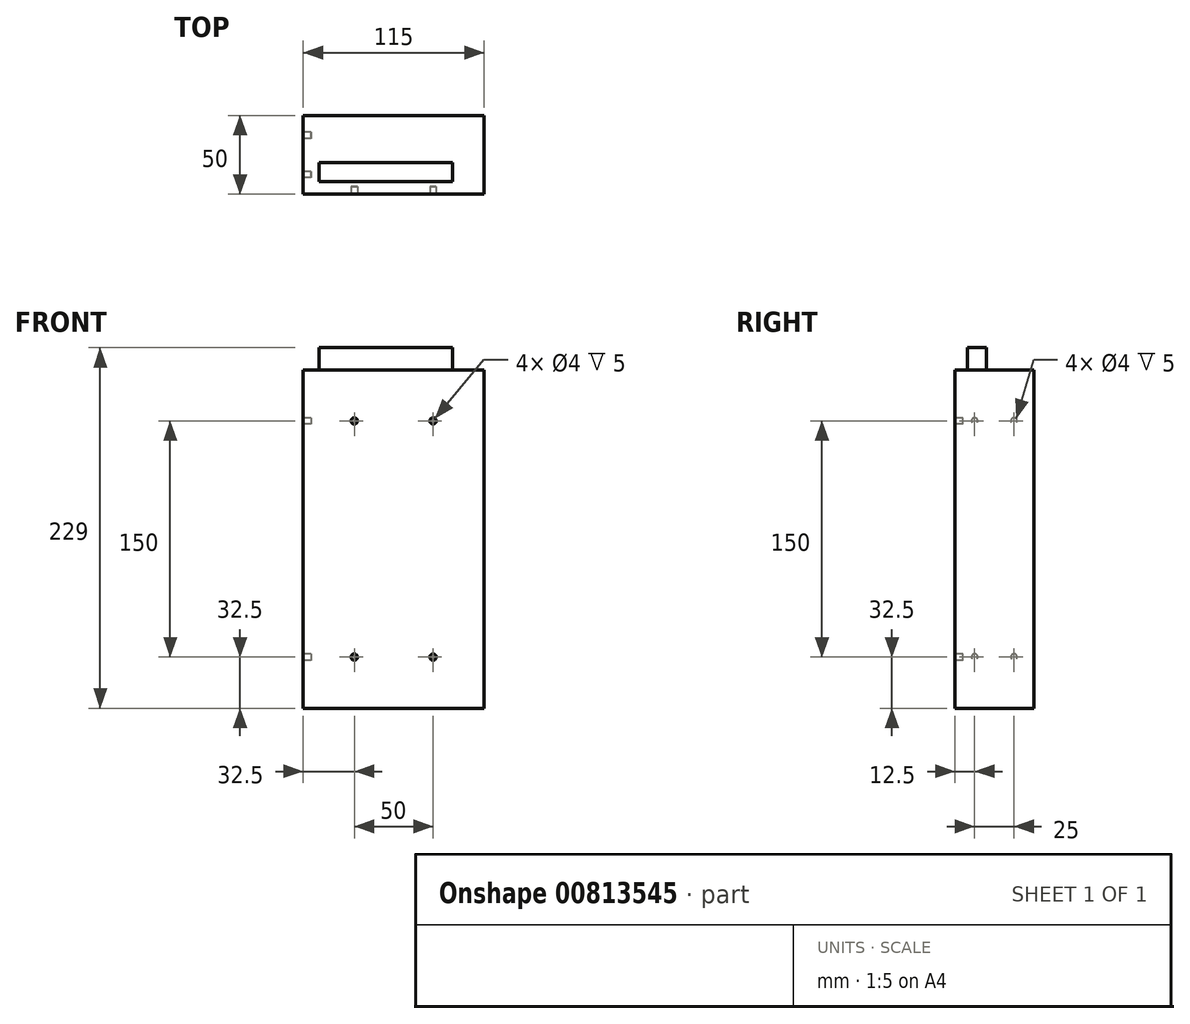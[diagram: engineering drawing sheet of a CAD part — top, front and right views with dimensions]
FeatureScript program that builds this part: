
annotation { "Feature Type Name" : "Feature", "Feature Type Description" : "" }
export const myFeature = defineFeature(function(context is Context, id is Id, definition is map)
    precondition{}
    {
        {
            var Q0;
            Q0=qCreatedBy(makeId("Front.planeOp"),FACE);
            var sketch = newSketch(context, id + "F0", { "sketchPlane" : qUnion([Q0])});
            skLineSegment(sketch, "E0.bottom", {"start": v(0, 0) * mm, "end": v(115, 0) * mm});
            skLineSegment(sketch, "E0.top", {"start": v(0, 215) * mm, "end": v(115, 215) * mm});
            skLineSegment(sketch, "E0.left", {"start": v(0, 0) * mm, "end": v(0, 215) * mm});
            skLineSegment(sketch, "E0.right", {"start": v(115, 0) * mm, "end": v(115, 215) * mm});
            skSolve(sketch);
        }
        {
            var Q0;
            Q0=makeQuery(id+"F0.imprint","IMPRINT",FACE,{"disambiguationData":[TD([[makeQuery(id+"F0.imprint","IMPRINT",EDGE,{"derivedFrom":sQuery(id+"F0.wireOp",EDGE,"E0.bottom")}),1.0]])]});
            extrude(context, id + "F1", {"entities" : qUnion([Q0]), "depth" : 50 * mm, "offsetDistance" : 25 * mm});
        }
        {
            var Q0;
            Q0=makeQuery(id+"F1.opExtrude","SWEPT_FACE",FACE,{"disambiguationData":[OSD([sQuery(id+"F0.wireOp",EDGE,"E0.top")])]});
            var sketch = newSketch(context, id + "F2", { "sketchPlane" : qUnion([Q0])});
            skLineSegment(sketch, "E1.bottom", {"start": v(10, -30) * mm, "end": v(95, -30) * mm});
            skLineSegment(sketch, "E1.top", {"start": v(10, -42) * mm, "end": v(95, -42) * mm});
            skLineSegment(sketch, "E1.left", {"start": v(10, -30) * mm, "end": v(10, -42) * mm});
            skLineSegment(sketch, "E1.right", {"start": v(95, -30) * mm, "end": v(95, -42) * mm});
            skSolve(sketch);
        }
        {
            var Q0;
            Q0=makeQuery(id+"F2.imprint","IMPRINT",FACE,{"disambiguationData":[TD([[makeQuery(id+"F2.imprint","IMPRINT",EDGE,{"derivedFrom":sQuery(id+"F2.wireOp",EDGE,"E1.bottom")}),-1.0]])]});
            extrude(context, id + "F3", {"entities" : qUnion([Q0]), "operationType" : NewBodyOperationType.ADD, "depth" : 14 * mm, "offsetDistance" : 25 * mm});
        }
        {
            var Q0;
            Q0=makeQuery(id+"F1.opExtrude","CAP_FACE",FACE,{"disambiguationData":[OSD([sQuery(id+"F0.wireOp",EDGE,"E0.bottom"),sQuery(id+"F0.wireOp",EDGE,"E0.top"),sQuery(id+"F0.wireOp",EDGE,"E0.left"),sQuery(id+"F0.wireOp",EDGE,"E0.right")])],"isStart":false});
            var sketch = newSketch(context, id + "F4", { "sketchPlane" : qUnion([Q0])});
            skLineSegment(sketch, "E2", {"start": v(57.5, 215) * mm, "end": v(57.5, 32.5) * mm, "construction": true});
            skLineSegment(sketch, "E3.bottom", {"start": v(32.5, 182.5) * mm, "end": v(82.5, 182.5) * mm, "construction": true});
            skLineSegment(sketch, "E3.top", {"start": v(32.5, 32.5) * mm, "end": v(82.5, 32.5) * mm, "construction": true});
            skLineSegment(sketch, "E3.left", {"start": v(32.5, 182.5) * mm, "end": v(32.5, 32.5) * mm, "construction": true});
            skLineSegment(sketch, "E3.right", {"start": v(82.5, 182.5) * mm, "end": v(82.5, 32.5) * mm, "construction": true});
            skCircle(sketch, "E4", {"center": v(32.5, 182.5) * mm, "radius": 2 * mm});
            skCircle(sketch, "E5", {"center": v(82.5, 182.5) * mm, "radius": 2 * mm});
            skCircle(sketch, "E6", {"center": v(82.5, 32.5) * mm, "radius": 2 * mm});
            skCircle(sketch, "E7", {"center": v(32.5, 32.5) * mm, "radius": 2 * mm});
            skSolve(sketch);
        }
        {
            var Q0;
            Q0=qSketchRegion(id+"F4",true);
            extrude(context, id + "F5", {"entities" : qUnion([Q0]), "operationType" : NewBodyOperationType.REMOVE, "oppositeDirection" : true, "depth" : 5 * mm, "offsetDistance" : 25 * mm});
        }
        {
            var Q0;
            Q0=makeQuery(id+"F1.opExtrude","SWEPT_FACE",FACE,{"disambiguationData":[OSD([sQuery(id+"F0.wireOp",EDGE,"E0.left")])]});
            var sketch = newSketch(context, id + "F6", { "sketchPlane" : qUnion([Q0])});
            skLineSegment(sketch, "E8", {"start": v(25, 215) * mm, "end": v(25, 189.6) * mm, "construction": true});
            skLineSegment(sketch, "E9", {"start": v(50, 107.5) * mm, "end": v(38.62, 107.5) * mm, "construction": true});
            skCircle(sketch, "E10", {"center": v(12.5, 182.5) * mm, "radius": 2 * mm});
            skCircle(sketch, "E11.MirrorC", {"center": v(37.5, 182.5) * mm, "radius": 2 * mm});
            skCircle(sketch, "E12.MirrorC", {"center": v(37.5, 32.5) * mm, "radius": 2 * mm});
            skCircle(sketch, "E13.MirrorC", {"center": v(12.5, 32.5) * mm, "radius": 2 * mm});
            skSolve(sketch);
        }
        {
            var Q0;
            Q0=qSketchRegion(id+"F6",true);
            extrude(context, id + "F7", {"entities" : qUnion([Q0]), "operationType" : NewBodyOperationType.REMOVE, "oppositeDirection" : true, "depth" : 5 * mm, "offsetDistance" : 25 * mm});
        }
    });
